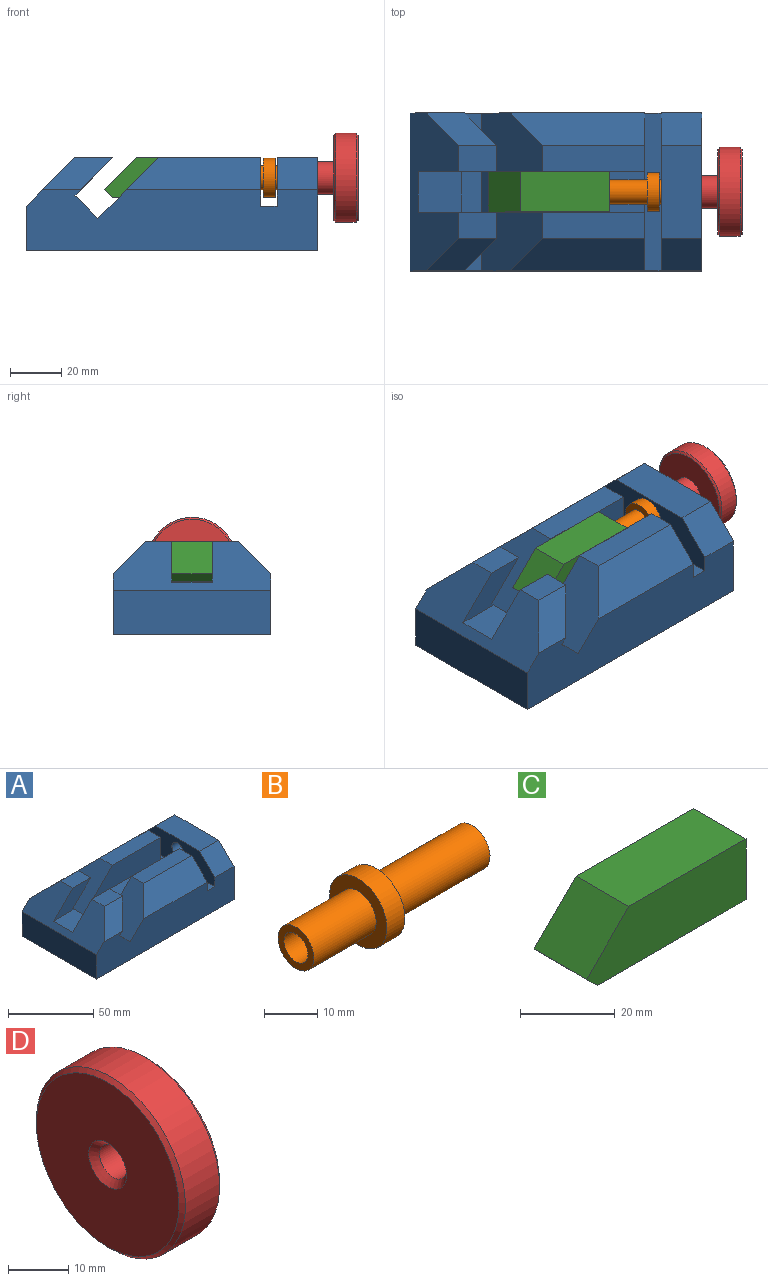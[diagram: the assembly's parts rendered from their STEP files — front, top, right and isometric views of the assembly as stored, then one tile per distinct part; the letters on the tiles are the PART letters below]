
ASSEMBLY  parts=4 mates=4
PART A: 31 faces, bbox 114.3x61.9x36.5 mm
  f0: plane 40.08x10.31mm, normal (0,0,1), area 413.3mm2, adj f2,f3,f22,f26
  f1: plane 14.99x10.31mm, normal (0,0,1), area 154.5mm2, adj f5,f20,f24,f28
  f2: plane 61.93x19.05mm, normal (1,0,0), area 766mm2, adj f0,f11,f12,f15,f16,f21,f22,f23
  f3: plane 61.93x23.83mm, normal (-0.71,0,0.71), area 1501.4mm2, adj f0,f4,f12,f15,f16,f21,f22,f23
  f4: plane 61.93x8.98mm, normal (0.71,0,0.71), area 763.3mm2, adj f3,f5,f6,f15,f16,f18,f19,f20
  f5: plane 23.01x14.85mm, normal (0.71,0,-0.71), area 369.1mm2, adj f1,f4,f16,f20,f28
  f6: plane 23.01x14.85mm, normal (0.71,0,-0.71), area 369.1mm2, adj f4,f13,f15,f19,f27
  f7: plane 61.93x17.48mm, normal (-1,0,0), area 1082.2mm2, adj f14,f15,f16,f24
  f8: plane 61.93x36.53mm, normal (1,0,0), area 2029.3mm2, adj f9,f14,f15,f16,f17,f25,f30
  f9: plane 36.53x15.88mm, normal (0,0,1), area 579.8mm2, adj f8,f10,f25,f30
  f10: plane 61.93x19.05mm, normal (-1,0,0), area 947.1mm2, adj f9,f11,f15,f16,f17,f25,f30
  f11: plane 61.93x6.35mm, normal (0,0,1), area 393.2mm2, adj f2,f10,f15,f16
  f12: plane 40.08x10.31mm, normal (0,0,1), area 413.3mm2, adj f2,f3,f21,f29
  f13: plane 14.99x10.31mm, normal (0,0,1), area 154.5mm2, adj f6,f19,f24,f27
  f14: plane 114.3x61.93mm, normal (0,0,-1), area 7078.1mm2, adj f7,f8,f15,f16
  f15: plane 114.3x23.83mm, normal (0,1,0), area 2543.6mm2, adj f2,f3,f4,f6,f7,f8,f10,f11
  f16: plane 114.3x23.83mm, normal (0,-1,0), area 2543.6mm2, adj f2,f3,f4,f5,f7,f8,f10,f11
  f17: cylinder r=4.76mm len=15.88mm, axis (1,0,0), area 475mm2, adj f8,f10
  f18: plane 17.05x15.9mm, normal (0,0,1), area 271mm2, adj f4,f19,f20,f24
  f19: plane 30.86x15.88mm, normal (0,-1,0), area 239mm2, adj f4,f6,f13,f18,f24
  f20: plane 30.86x15.88mm, normal (0,1,0), area 239mm2, adj f1,f4,f5,f18,f24
  f21: plane 55.95x15.88mm, normal (0,1,0), area 762.3mm2, adj f2,f3,f12,f23
  f22: plane 55.95x15.88mm, normal (0,-1,0), area 762.3mm2, adj f0,f2,f3,f23
  f23: plane 55.95x15.9mm, normal (0,0,1), area 889.7mm2, adj f2,f3,f21,f22
  f24: plane 61.93x19.05mm, normal (-0.71,0,0.71), area 1083.2mm2, adj f1,f7,f13,f15,f16,f18,f19,f20
  f25: plane 15.88x12.7mm, normal (0,0.71,0.71), area 285.1mm2, adj f8,f9,f10,f15
  f26: plane 52.78x12.7mm, normal (0,0.71,0.71), area 833.9mm2, adj f0,f2,f3,f15
  f27: plane 27.69x12.7mm, normal (0,0.71,0.71), area 269.2mm2, adj f6,f13,f15,f24
  f28: plane 27.69x12.7mm, normal (0,-0.71,0.71), area 269.2mm2, adj f1,f5,f16,f24
  f29: plane 52.78x12.7mm, normal (0,-0.71,0.71), area 833.9mm2, adj f2,f3,f12,f16
  f30: plane 15.88x12.7mm, normal (0,-0.71,0.71), area 285.1mm2, adj f8,f9,f10,f16
PART B: 9 faces, bbox 46.7x15.2x15.2 mm
  f0: cylinder r=4.76mm len=16.51mm, axis (-1,0,0), area 494mm2, adj f1,f4
  f1: plane 9.53x9.53mm, normal (-1,0,0), area 39.6mm2, adj f0,f7
  f2: cylinder r=7.62mm len=15.24mm, axis (-1,0,0), area 228.6mm2, adj f3,f4
  f3: plane 15.24x15.24mm, normal (1,0,0), area 111.2mm2, adj f2,f5
  f4: plane 15.24x15.24mm, normal (-1,0,0), area 111.2mm2, adj f0,f2
  f5: cylinder r=4.76mm len=25.4mm, axis (-1,0,0), area 760.1mm2, adj f3,f6
  f6: plane 9.53x9.53mm, normal (1,0,0), area 71.3mm2, adj f5
  f7: cylinder r=3.17mm len=12.7mm, axis (-1,0,0), area 253.4mm2, adj f1,f8
  f8: plane 6.35x6.35mm, normal (-1,0,0), area 31.7mm2, adj f7
PART C: 9 faces, bbox 47.6x15.7x15.7 mm
  f0: plane 15.75x3.18mm, normal (-0.71,0,-0.71), area 70.7mm2, adj f1,f4,f5,f6
  f1: plane 44.45x15.75mm, normal (0,0,-1), area 700mm2, adj f0,f2,f5,f6
  f2: plane 15.75x15.75mm, normal (1,0,0), area 176.7mm2, adj f1,f3,f5,f6,f7
  f3: plane 35.05x15.75mm, normal (0,0,1), area 552mm2, adj f2,f4,f5,f6
  f4: plane 15.75x12.57mm, normal (-0.71,0,0.71), area 280mm2, adj f0,f3,f5,f6
  f5: plane 47.63x15.75mm, normal (0,1,0), area 665.9mm2, adj f0,f1,f2,f3,f4
  f6: plane 47.63x15.75mm, normal (0,-1,0), area 665.9mm2, adj f0,f1,f2,f3,f4
  f7: cylinder r=4.76mm len=25.4mm, axis (1,0,0), area 760.1mm2, adj f2,f8
  f8: plane 9.53x9.53mm, normal (1,0,0), area 71.3mm2, adj f7
PART D: 9 faces, bbox 15.9x34.9x34.9 mm
  f0: cylinder r=17.46mm len=34.93mm, axis (1,0,0), area 877.9mm2, adj f7,f8
  f1: plane 33.4x33.4mm, normal (-1,0,0), area 814.1mm2, adj f6,f8
  f2: plane 33.4x33.4mm, normal (1,0,0), area 749.5mm2, adj f3,f7
  f3: cylinder r=6.35mm len=12.7mm, axis (-1,0,0), area 253.4mm2, adj f2,f4
  f4: plane 12.7x12.7mm, normal (1,0,0), area 95mm2, adj f3,f5
  f5: cylinder r=3.17mm len=14.61mm, axis (1,0,0), area 291.4mm2, adj f4,f6
  f6: cone r=4.45mm half-angle=45deg, axis (-1,0,0), area 43mm2, adj f1,f5
  f7: cone r=16.7mm half-angle=45deg, axis (-1,0,0), area 115.7mm2, adj f0,f2
  f8: cone r=17.46mm half-angle=45deg, axis (1,0,0), area 115.7mm2, adj f0,f1
PLACE A at identity fixed
PLACE B rot(axis=(0,-0.59,-0.81),180deg) t=(114.3,30.96,28.58)mm
PLACE C t=(30.77,23.09,20.7)mm
PLACE D rot(axis=(0,-0.59,-0.81),180deg) t=(120.65,30.96,28.58)mm
MATE slider C.f7 <-> A.f17  axis (1,0,0) through (78.39,30.96,28.58)mm
MATE revolute B.f7 <-> A.f17  axis (1,0,0) through (114.3,30.96,28.58)mm
MATE cylindrical C.f7 <-> B.f5  axis (1,0,0) through (78.39,30.96,28.58)mm
MATE fastened D.f5 <-> B.f7  axis (-1,0,0) through (114.3,30.96,28.58)mm
